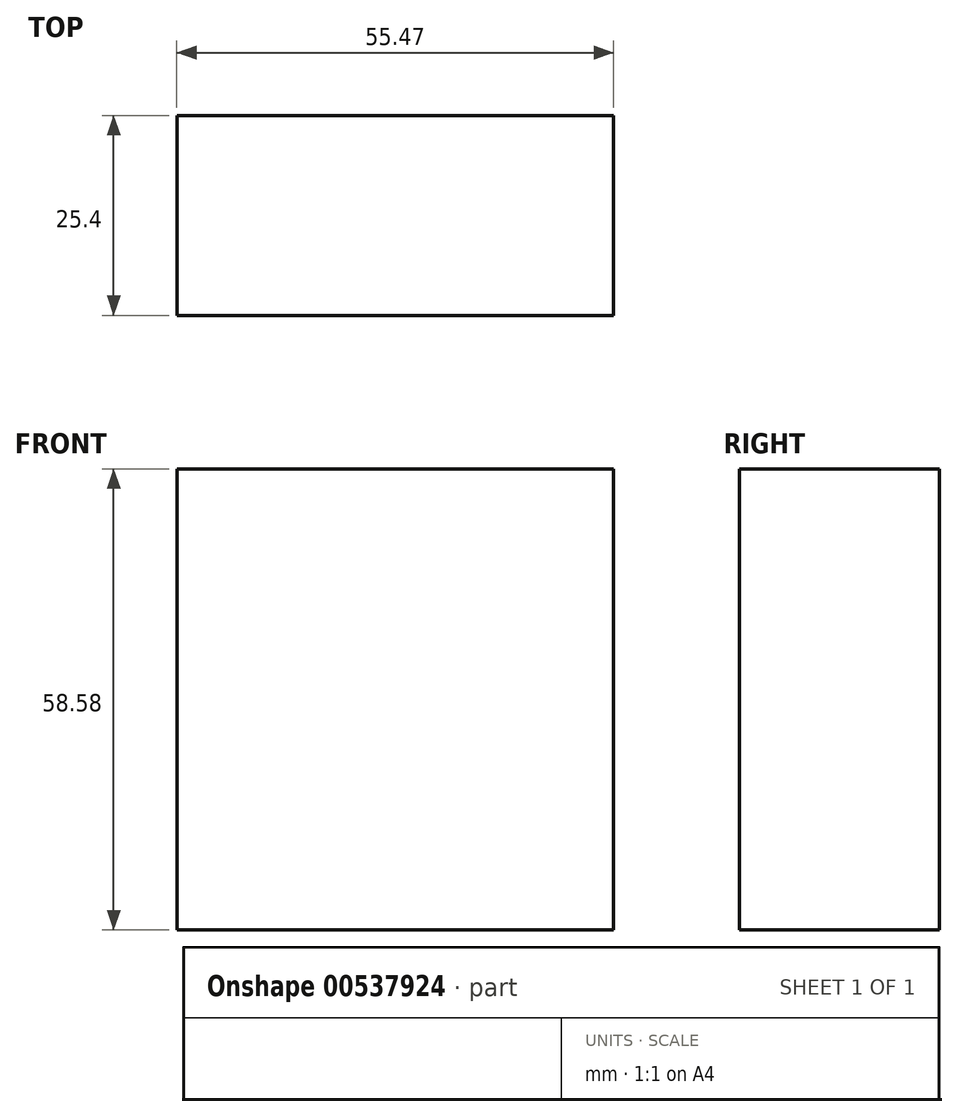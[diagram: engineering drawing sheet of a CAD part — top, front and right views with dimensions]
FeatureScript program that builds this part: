
annotation { "Feature Type Name" : "Feature", "Feature Type Description" : "" }
export const myFeature = defineFeature(function(context is Context, id is Id, definition is map)
    precondition{}
    {
        {
            var Q0;
            Q0=qCreatedBy(makeId("Front.planeOp"),FACE);
            var sketch = newSketch(context, id + "F0", { "sketchPlane" : qUnion([Q0])});
            skLineSegment(sketch, "E0.bottom", {"start": v(-24.35, 28.78) * mm, "end": v(31.12, 28.78) * mm});
            skLineSegment(sketch, "E0.top", {"start": v(-24.35, -29.8) * mm, "end": v(31.12, -29.8) * mm});
            skLineSegment(sketch, "E0.left", {"start": v(-24.35, 28.78) * mm, "end": v(-24.35, -29.8) * mm});
            skLineSegment(sketch, "E0.right", {"start": v(31.12, 28.78) * mm, "end": v(31.12, -29.8) * mm});
            skSolve(sketch);
        }
        {
            var Q0;
            Q0=makeQuery(id+"F0.imprint","IMPRINT",FACE,{"disambiguationData":[TD([[makeQuery(id+"F0.imprint","IMPRINT",EDGE,{"derivedFrom":sQuery(id+"F0.wireOp",EDGE,"E0.bottom")}),-1.0]])]});
            extrude(context, id + "F1", {"entities" : qUnion([Q0]), "depth" : 25.4 * mm, "offsetDistance" : 25.4 * mm});
        }
    });
